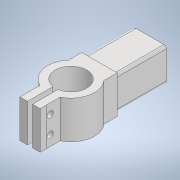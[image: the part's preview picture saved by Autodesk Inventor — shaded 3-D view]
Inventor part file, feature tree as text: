
AUTODESK INVENTOR PART (.ipt)
format: ipt  version: 2020 (Build 240168000, 168)  size: 272,384 bytes
history: native  units: mm
features: sketch x12, extrude x11, hole x1
ambient origin geometry x8: Origin, YZ Plane, XZ Plane, XY Plane, X Axis, Y Axis, Z Axis, Center Point
bodies: Solido1 (feature_tree)
feature tree (24):
  extrude  "Estrusione1"  Depth=18.0mm
  extrude  "Estrusione2"  Depth=40.0mm TaperAngle=0.0deg
  extrude  "Estrusione3"  Depth=30.0mm
  extrude  "Estrusione4"  Depth=37.0mm
  extrude  "Estrusione5"  Depth=50.0mm TaperAngle=0.0deg
  extrude  "Estrusione6"  Depth=22.5mm
  extrude  "Estrusione7"  TaperAngle=90.0deg  [1 undecoded]
  extrude  "Estrusione8"  Depth=25.0mm
  extrude  "Estrusione9"  Depth=30.0mm TaperAngle=0.0deg
  hole  "Foro1"  [1 undecoded]
  extrude  "Estrusione10"  Depth=2.0mm
  extrude  "Estrusione11"  TaperAngle=0.0deg  [1 undecoded]
  sketch  "Schizzo1"
  sketch  "Schizzo2"
  sketch  "Schizzo3"
  sketch  "Schizzo4"
  sketch  "Schizzo5"
  sketch  "Schizzo6"
  sketch  "Schizzo7"
  sketch  "Schizzo8"
  sketch  "Schizzo10"
  sketch  "Schizzo11"
  sketch  "Schizzo14"
  sketch  "Schizzo15"
note: 3 required parameter values undecoded (feature->parameter linkage not recoverable at this tier; creation-order binding heuristic only, values carry confidence <= 0.55)
